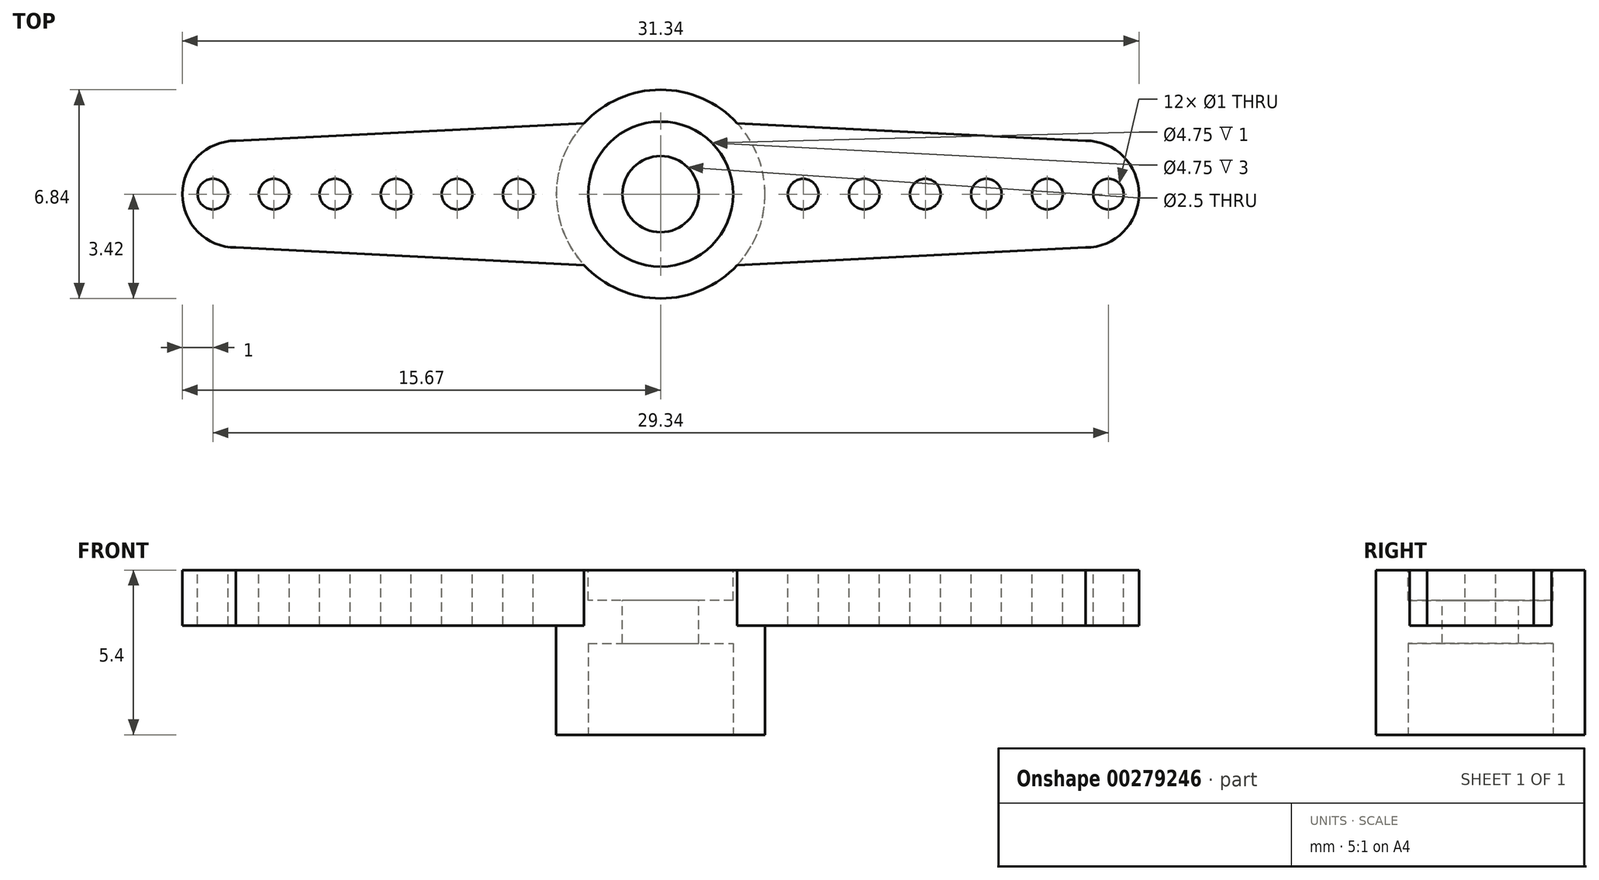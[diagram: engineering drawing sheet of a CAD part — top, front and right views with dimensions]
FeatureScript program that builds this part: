
annotation { "Feature Type Name" : "Feature", "Feature Type Description" : "" }
export const myFeature = defineFeature(function(context is Context, id is Id, definition is map)
    precondition{}
    {
        {
            var Q0;
            Q0=qCreatedBy(makeId("Top.planeOp"),FACE);
            var sketch = newSketch(context, id + "F0", { "sketchPlane" : qUnion([Q0])});
            skCircle(sketch, "E0", {"center": v(-13.92, 0) * mm, "radius": 1.75 * mm});
            skCircle(sketch, "E1.MirrorC", {"center": v(13.92, 0) * mm, "radius": 1.75 * mm});
            skLineSegment(sketch, "E2", {"start": v(-13.92, 1.75) * mm, "end": v(-13.92, -1.75) * mm});
            skLineSegment(sketch, "E3", {"start": v(-13.92, 1.75) * mm, "end": v(0, 2.45) * mm});
            skLineSegment(sketch, "E4", {"start": v(-13.92, -1.75) * mm, "end": v(0, -2.45) * mm});
            skLineSegment(sketch, "E5.MirrorCS", {"start": v(13.92, 1.75) * mm, "end": v(0, 2.45) * mm});
            skLineSegment(sketch, "E6.MirrorCS", {"start": v(13.92, -1.75) * mm, "end": v(0, -2.45) * mm});
            skLineSegment(sketch, "E7.MirrorCS", {"start": v(13.92, 1.75) * mm, "end": v(13.92, -1.75) * mm});
            skLineSegment(sketch, "E8", {"start": v(0, 2.45) * mm, "end": v(0, -2.45) * mm});
            skSolve(sketch);
        }
        {
            var Q0;
            {var subQ0=sQuery(id+"F0.wireOp",EDGE,"E2");Q0=makeQuery(id+"F0.imprint","IMPRINT",FACE,{"disambiguationData":[TD([[makeQuery(id+"F0.imprint","IMPRINT",EDGE,{"derivedFrom":subQ0}),-1.0]])]});}
            var Q1;
            {var subQ0=sQuery(id+"F0.wireOp",EDGE,"E2");Q1=makeQuery(id+"F0.imprint","IMPRINT",FACE,{"disambiguationData":[TD([[makeQuery(id+"F0.imprint","IMPRINT",EDGE,{"derivedFrom":subQ0}),1.0]])]});}
            var Q2;
            {var subQ0=sQuery(id+"F0.wireOp",EDGE,"E3");Q2=makeQuery(id+"F0.imprint","IMPRINT",FACE,{"disambiguationData":[TD([[makeQuery(id+"F0.imprint","IMPRINT",EDGE,{"derivedFrom":subQ0}),-1.0]])]});}
            var Q3;
            {var subQ1=sQuery(id+"F0.wireOp",EDGE,"E5.MirrorCS");Q3=makeQuery(id+"F0.imprint","IMPRINT",FACE,{"disambiguationData":[TD([[makeQuery(id+"F0.imprint","IMPRINT",EDGE,{"derivedFrom":subQ1}),1.0]])]});}
            var Q4;
            {var subQ0=sQuery(id+"F0.wireOp",EDGE,"E7.MirrorCS");Q4=makeQuery(id+"F0.imprint","IMPRINT",FACE,{"disambiguationData":[TD([[makeQuery(id+"F0.imprint","IMPRINT",EDGE,{"derivedFrom":subQ0}),-1.0]])]});}
            var Q5;
            {var subQ0=sQuery(id+"F0.wireOp",EDGE,"E7.MirrorCS");Q5=makeQuery(id+"F0.imprint","IMPRINT",FACE,{"disambiguationData":[TD([[makeQuery(id+"F0.imprint","IMPRINT",EDGE,{"derivedFrom":subQ0}),1.0]])]});}
            extrude(context, id + "F1", {"entities" : qUnion([Q0, Q1, Q2, Q3, Q4, Q5]), "endBound" : BoundingType.SYMMETRIC, "oppositeDirection" : true, "depth" : 1.82 * mm});
        }
        {
            var Q0;
            Q0=makeQuery(id+"F1.opExtrude","CAP_FACE",FACE,{"disambiguationData":[OSD([sQuery(id+"F0.wireOp",EDGE,"E0"),sQuery(id+"F0.wireOp",EDGE,"E1.MirrorC"),sQuery(id+"F0.wireOp",EDGE,"E3"),sQuery(id+"F0.wireOp",EDGE,"E4"),sQuery(id+"F0.wireOp",EDGE,"E5.MirrorCS"),sQuery(id+"F0.wireOp",EDGE,"E6.MirrorCS")])],"isStart":true});
            var sketch = newSketch(context, id + "F2", { "sketchPlane" : qUnion([Q0])});
            skCircle(sketch, "E9", {"center": v(0, 0) * mm, "radius": 3.42 * mm});
            skSolve(sketch);
        }
        {
            var Q0;
            {var subQ0=sQuery(id+"F2.wireOp",EDGE,"E9");var subQ1=makeQuery(id+"F1.opExtrude","CAP_EDGE",EDGE,{"disambiguationData":[OSD([sQuery(id+"F0.wireOp",EDGE,"E3")])],"isStart":true});var subQ2=makeQuery(id+"F2.imprint","INTERSECT",VERTEX,{"derivedFrom":[subQ1,subQ0]});Q0=makeQuery(id+"F2.imprint","IMPRINT",FACE,{"disambiguationData":[TD([[makeQuery(id+"F2.imprint","IMPRINT",EDGE,{"disambiguationData":[TD([[subQ2,1.0]])],"derivedFrom":subQ0}),1.0]])]});}
            var Q1;
            {var subQ3=sQuery(id+"F2.wireOp",EDGE,"E9");var subQ6=makeQuery(id+"F1.opExtrude","CAP_EDGE",EDGE,{"disambiguationData":[OSD([sQuery(id+"F0.wireOp",EDGE,"E3")])],"isStart":true});var subQ8=makeQuery(id+"F2.imprint","INTERSECT",VERTEX,{"derivedFrom":[subQ6,subQ3]});Q1=makeQuery(id+"F2.imprint","IMPRINT",FACE,{"disambiguationData":[TD([[makeQuery(id+"F2.imprint","IMPRINT",EDGE,{"disambiguationData":[TD([[subQ8,-1.0]])],"derivedFrom":subQ3}),1.0]])]});}
            var Q2;
            {var subQ0=sQuery(id+"F2.wireOp",EDGE,"E9");var subQ1=makeQuery(id+"F1.opExtrude","CAP_EDGE",EDGE,{"disambiguationData":[OSD([sQuery(id+"F0.wireOp",EDGE,"E4")])],"isStart":true});var subQ2=makeQuery(id+"F2.imprint","INTERSECT",VERTEX,{"derivedFrom":[subQ1,subQ0]});Q2=makeQuery(id+"F2.imprint","IMPRINT",FACE,{"disambiguationData":[TD([[makeQuery(id+"F2.imprint","IMPRINT",EDGE,{"disambiguationData":[TD([[subQ2,-1.0]])],"derivedFrom":subQ0}),1.0]])]});}
            extrude(context, id + "F3", {"entities" : qUnion([Q0, Q1, Q2]), "operationType" : NewBodyOperationType.ADD, "oppositeDirection" : true, "depth" : 5.4 * mm});
        }
        {
            var Q0;
            Q0=makeQuery(id+"F3.boolean.opBoolean","MERGE",FACE,{"derivedFrom":[makeQuery(id+"F1.opExtrude","CAP_FACE",FACE,{"disambiguationData":[OSD([sQuery(id+"F0.wireOp",EDGE,"E0"),sQuery(id+"F0.wireOp",EDGE,"E1.MirrorC"),sQuery(id+"F0.wireOp",EDGE,"E3"),sQuery(id+"F0.wireOp",EDGE,"E4"),sQuery(id+"F0.wireOp",EDGE,"E5.MirrorCS"),sQuery(id+"F0.wireOp",EDGE,"E6.MirrorCS")])],"isStart":true}),makeQuery(id+"F3.opExtrude","CAP_FACE",FACE,{"disambiguationData":[OSD([sQuery(id+"F2.wireOp",EDGE,"E9")])],"isStart":true})]});
            var sketch = newSketch(context, id + "F4", { "sketchPlane" : qUnion([Q0])});
            skCircle(sketch, "E10", {"center": v(0, 0) * mm, "radius": 2.38 * mm});
            skSolve(sketch);
        }
        {
            var Q0;
            Q0=makeQuery(id+"F4.imprint","IMPRINT",FACE,{"disambiguationData":[TD([[makeQuery(id+"F4.imprint","IMPRINT",EDGE,{"derivedFrom":sQuery(id+"F4.wireOp",EDGE,"E10")}),1.0]])]});
            extrude(context, id + "F5", {"entities" : qUnion([Q0]), "operationType" : NewBodyOperationType.REMOVE, "oppositeDirection" : true, "depth" : 1 * mm});
        }
        {
            var Q0;
            Q0=makeQuery(id+"F3.opExtrude","CAP_FACE",FACE,{"disambiguationData":[OSD([sQuery(id+"F2.wireOp",EDGE,"E9")])],"isStart":false});
            var sketch = newSketch(context, id + "F6", { "sketchPlane" : qUnion([Q0])});
            skCircle(sketch, "E11", {"center": v(0, 0) * mm, "radius": 2.38 * mm});
            skSolve(sketch);
        }
        {
            var Q0;
            Q0=makeQuery(id+"F6.imprint","IMPRINT",FACE,{"disambiguationData":[TD([[makeQuery(id+"F6.imprint","IMPRINT",EDGE,{"derivedFrom":sQuery(id+"F6.wireOp",EDGE,"E11")}),1.0]])]});
            extrude(context, id + "F7", {"entities" : qUnion([Q0]), "operationType" : NewBodyOperationType.REMOVE, "oppositeDirection" : true, "depth" : 3 * mm});
        }
        {
            var Q0;
            Q0=makeQuery(id+"F5.boolean.opBoolean","COPY",FACE,{"derivedFrom":makeQuery(id+"F5.opExtrude","CAP_FACE",FACE,{"disambiguationData":[OSD([sQuery(id+"F4.wireOp",EDGE,"E10")])],"isStart":false})});
            var sketch = newSketch(context, id + "F8", { "sketchPlane" : qUnion([Q0])});
            skCircle(sketch, "E12", {"center": v(0, 0) * mm, "radius": 1.25 * mm});
            skSolve(sketch);
        }
        {
            var Q0;
            Q0=sQuery(id+"F8.wireOp",VERTEX,"E12.center");
            var Q1;
            Q1=makeQuery(id+"F1.opExtrude","SWEPT_BODY",BODY,{"disambiguationData":[OSD([sQuery(id+"F0.wireOp",EDGE,"E0"),sQuery(id+"F0.wireOp",EDGE,"E1.MirrorC"),sQuery(id+"F0.wireOp",EDGE,"E3"),sQuery(id+"F0.wireOp",EDGE,"E4"),sQuery(id+"F0.wireOp",EDGE,"E5.MirrorCS"),sQuery(id+"F0.wireOp",EDGE,"E6.MirrorCS")])]});
            hole(context, id + "F9", {"style" : HoleStyle.SIMPLE, "endStyle" : HoleEndStyle.THROUGH, "holeDiameter" : 2.5 * mm, "tappedDepth" : 12 * mm, "tapClearance" : 3, "locations" : qUnion([Q0]), "scope" : qUnion([Q1])});
        }
        {
            var Q0;
            Q0=makeQuery(id+"F3.boolean.opBoolean","MERGE",FACE,{"derivedFrom":[makeQuery(id+"F1.opExtrude","CAP_FACE",FACE,{"disambiguationData":[OSD([sQuery(id+"F0.wireOp",EDGE,"E0"),sQuery(id+"F0.wireOp",EDGE,"E1.MirrorC"),sQuery(id+"F0.wireOp",EDGE,"E3"),sQuery(id+"F0.wireOp",EDGE,"E4"),sQuery(id+"F0.wireOp",EDGE,"E5.MirrorCS"),sQuery(id+"F0.wireOp",EDGE,"E6.MirrorCS")])],"isStart":true}),makeQuery(id+"F3.opExtrude","CAP_FACE",FACE,{"disambiguationData":[OSD([sQuery(id+"F2.wireOp",EDGE,"E9")])],"isStart":true})]});
            var sketch = newSketch(context, id + "F10", { "sketchPlane" : qUnion([Q0])});
            skCircle(sketch, "E13", {"center": v(-14.67, 0) * mm, "radius": 0.5 * mm});
            skCircle(sketch, "E14", {"center": v(-12.67, 0) * mm, "radius": 0.5 * mm});
            skCircle(sketch, "E15", {"center": v(-10.67, 0) * mm, "radius": 0.5 * mm});
            skCircle(sketch, "E16", {"center": v(-8.67, 0) * mm, "radius": 0.5 * mm});
            skCircle(sketch, "E17", {"center": v(-6.67, 0) * mm, "radius": 0.5 * mm});
            skCircle(sketch, "E18", {"center": v(-4.67, 0) * mm, "radius": 0.5 * mm});
            skCircle(sketch, "E19.MirrorC", {"center": v(14.67, 0) * mm, "radius": 0.5 * mm});
            skCircle(sketch, "E20.MirrorC", {"center": v(12.67, 0) * mm, "radius": 0.5 * mm});
            skCircle(sketch, "E21.MirrorC", {"center": v(10.67, 0) * mm, "radius": 0.5 * mm});
            skCircle(sketch, "E22.MirrorC", {"center": v(8.67, 0) * mm, "radius": 0.5 * mm});
            skCircle(sketch, "E23.MirrorC", {"center": v(6.67, 0) * mm, "radius": 0.5 * mm});
            skCircle(sketch, "E24.MirrorC", {"center": v(4.67, 0) * mm, "radius": 0.5 * mm});
            skSolve(sketch);
        }
        {
            var Q0;
            Q0=sQuery(id+"F10.wireOp",VERTEX,"E13.center");
            var Q1;
            Q1=sQuery(id+"F10.wireOp",VERTEX,"E14.center");
            var Q2;
            Q2=sQuery(id+"F10.wireOp",VERTEX,"E15.center");
            var Q3;
            Q3=sQuery(id+"F10.wireOp",VERTEX,"E16.center");
            var Q4;
            Q4=sQuery(id+"F10.wireOp",VERTEX,"E17.center");
            var Q5;
            Q5=sQuery(id+"F10.wireOp",VERTEX,"E18.center");
            var Q6;
            Q6=sQuery(id+"F10.wireOp",VERTEX,"E24.MirrorC.center");
            var Q7;
            Q7=sQuery(id+"F10.wireOp",VERTEX,"E23.MirrorC.center");
            var Q8;
            Q8=sQuery(id+"F10.wireOp",VERTEX,"E22.MirrorC.center");
            var Q9;
            Q9=sQuery(id+"F10.wireOp",VERTEX,"E21.MirrorC.center");
            var Q10;
            Q10=sQuery(id+"F10.wireOp",VERTEX,"E20.MirrorC.center");
            var Q11;
            Q11=sQuery(id+"F10.wireOp",VERTEX,"E19.MirrorC.center");
            var Q12;
            Q12=makeQuery(id+"F1.opExtrude","SWEPT_BODY",BODY,{"disambiguationData":[OSD([sQuery(id+"F0.wireOp",EDGE,"E0"),sQuery(id+"F0.wireOp",EDGE,"E1.MirrorC"),sQuery(id+"F0.wireOp",EDGE,"E3"),sQuery(id+"F0.wireOp",EDGE,"E4"),sQuery(id+"F0.wireOp",EDGE,"E5.MirrorCS"),sQuery(id+"F0.wireOp",EDGE,"E6.MirrorCS")])]});
            hole(context, id + "F11", {"style" : HoleStyle.SIMPLE, "endStyle" : HoleEndStyle.THROUGH, "holeDiameter" : 1 * mm, "tappedDepth" : 12 * mm, "tapClearance" : 3, "locations" : qUnion([Q0, Q1, Q2, Q3, Q4, Q5, Q6, Q7, Q8, Q9, Q10, Q11]), "scope" : qUnion([Q12])});
        }
    });
